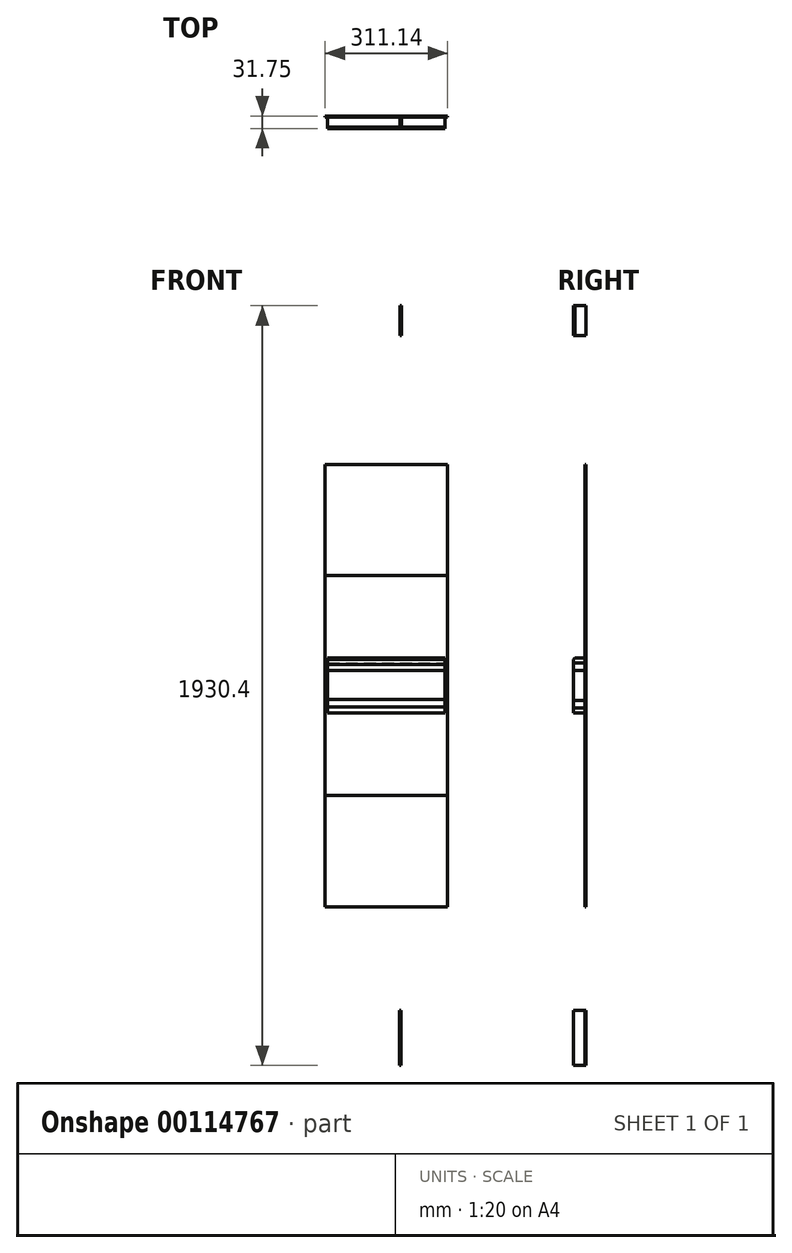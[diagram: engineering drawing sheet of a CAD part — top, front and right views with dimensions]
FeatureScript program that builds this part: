
annotation { "Feature Type Name" : "Feature", "Feature Type Description" : "" }
export const myFeature = defineFeature(function(context is Context, id is Id, definition is map)
    precondition{}
    {
        {
            var Q0;
            Q0=qCreatedBy(makeId("Front.planeOp"),FACE);
            var sketch = newSketch(context, id + "F0", { "sketchPlane" : qUnion([Q0])});
            skLineSegment(sketch, "E0.bottom", {"start": v(38.1, 965.2) * mm, "end": v(-38.1, 965.2) * mm});
            skLineSegment(sketch, "E0.top", {"start": v(38.1, -965.2) * mm, "end": v(-38.1, -965.2) * mm});
            skLineSegment(sketch, "E0.left", {"start": v(38.1, 965.2) * mm, "end": v(38.1, -965.2) * mm});
            skLineSegment(sketch, "E0.right", {"start": v(-38.1, 965.2) * mm, "end": v(-38.1, -965.2) * mm});
            skPoint(sketch, "E0.middle", {"position": v(0, 0) * mm});
            skLineSegment(sketch, "E1.bottom", {"start": v(38.1, -279.4) * mm, "end": v(38.1, -279.4) * mm});
            skLineSegment(sketch, "E2.bottom", {"start": v(38.1, -279.4) * mm, "end": v(34.93, -279.4) * mm});
            skLineSegment(sketch, "E2.top", {"start": v(38.1, -165.1) * mm, "end": v(34.93, -165.1) * mm});
            skLineSegment(sketch, "E2.left", {"start": v(38.1, -279.4) * mm, "end": v(38.1, -165.1) * mm});
            skLineSegment(sketch, "E2.right", {"start": v(34.93, -279.4) * mm, "end": v(34.93, -165.1) * mm});
            skLineSegment(sketch, "E3.bottom", {"start": v(38.1, -965.2) * mm, "end": v(34.93, -965.2) * mm});
            skLineSegment(sketch, "E3.top", {"start": v(38.1, -825.5) * mm, "end": v(34.93, -825.5) * mm});
            skLineSegment(sketch, "E3.left", {"start": v(38.1, -965.2) * mm, "end": v(38.1, -825.5) * mm});
            skLineSegment(sketch, "E3.right", {"start": v(34.93, -965.2) * mm, "end": v(34.93, -825.5) * mm});
            skLineSegment(sketch, "E4.bottom", {"start": v(38.1, 965.2) * mm, "end": v(34.92, 965.2) * mm});
            skLineSegment(sketch, "E4.top", {"start": v(38.1, 889) * mm, "end": v(34.92, 889) * mm});
            skLineSegment(sketch, "E4.left", {"start": v(38.1, 965.2) * mm, "end": v(38.1, 889) * mm});
            skLineSegment(sketch, "E4.right", {"start": v(34.92, 965.2) * mm, "end": v(34.92, 889) * mm});
            skSolve(sketch);
        }
        {
            var Q0;
            Q0=makeQuery(id+"F0.imprint","IMPRINT",FACE,{"disambiguationData":[TD([[makeQuery(id+"F0.imprint","IMPRINT",EDGE,{"derivedFrom":sQuery(id+"F0.wireOp",EDGE,"E0.bottom")}),1.0]])]});
            extrude(context, id + "F1", {"entities" : qUnion([Q0]), "depth" : 31.75 * mm});
        }
        {
            var Q0;
            Q0=qCreatedBy(makeId("Front.planeOp"),FACE);
            var sketch = newSketch(context, id + "F2", { "sketchPlane" : qUnion([Q0])});
            skLineSegment(sketch, "E5.bottom", {"start": v(149.23, -69.85) * mm, "end": v(-149.22, -69.85) * mm});
            skLineSegment(sketch, "E5.top", {"start": v(149.23, 69.85) * mm, "end": v(-149.22, 69.85) * mm});
            skLineSegment(sketch, "E5.left", {"start": v(149.23, -69.85) * mm, "end": v(149.23, 69.85) * mm});
            skLineSegment(sketch, "E5.right", {"start": v(-149.22, -69.85) * mm, "end": v(-149.22, 69.85) * mm});
            skPoint(sketch, "E5.middle", {"position": v(0, 0) * mm});
            skSolve(sketch);
        }
        {
            var Q0;
            Q0=makeQuery(id+"F2.imprint","IMPRINT",FACE,{"disambiguationData":[TD([[makeQuery(id+"F2.imprint","IMPRINT",EDGE,{"derivedFrom":sQuery(id+"F2.wireOp",EDGE,"E5.bottom")}),-1.0]])]});
            extrude(context, id + "F3", {"entities" : qUnion([Q0]), "depth" : 31.75 * mm});
        }
        {
            var Q0;
            Q0=qCreatedBy(makeId("Front.planeOp"),FACE);
            var sketch = newSketch(context, id + "F4", { "sketchPlane" : qUnion([Q0])});
            skLineSegment(sketch, "E6.bottom", {"start": v(149.23, -38.1) * mm, "end": v(-149.23, -38.1) * mm});
            skLineSegment(sketch, "E6.top", {"start": v(149.23, 38.1) * mm, "end": v(-149.23, 38.1) * mm});
            skLineSegment(sketch, "E6.left", {"start": v(149.23, -38.1) * mm, "end": v(149.23, 38.1) * mm});
            skLineSegment(sketch, "E6.right", {"start": v(-149.23, -38.1) * mm, "end": v(-149.23, 38.1) * mm});
            skPoint(sketch, "E6.middle", {"position": v(0, 0) * mm});
            skSolve(sketch);
        }
        {
            var Q0;
            Q0=makeQuery(id+"F4.imprint","IMPRINT",FACE,{"disambiguationData":[TD([[makeQuery(id+"F4.imprint","IMPRINT",EDGE,{"derivedFrom":sQuery(id+"F4.wireOp",EDGE,"E6.bottom")}),-1.0]])]});
            extrude(context, id + "F5", {"entities" : qUnion([Q0]), "depth" : 31.75 * mm});
        }
        {
            var Q0;
            Q0=qCreatedBy(makeId("Front.planeOp"),FACE);
            var sketch = newSketch(context, id + "F6", { "sketchPlane" : qUnion([Q0])});
            skLineSegment(sketch, "E7.bottom", {"start": v(149.23, -57.15) * mm, "end": v(-149.23, -57.15) * mm});
            skLineSegment(sketch, "E7.top", {"start": v(149.22, 57.15) * mm, "end": v(-149.22, 57.15) * mm});
            skLineSegment(sketch, "E7.left", {"start": v(149.23, -57.15) * mm, "end": v(149.23, 57.15) * mm});
            skLineSegment(sketch, "E7.right", {"start": v(-149.23, -57.15) * mm, "end": v(-149.23, 57.15) * mm});
            skPoint(sketch, "E7.middle", {"position": v(0, 0) * mm});
            skSolve(sketch);
        }
        {
            var Q0;
            Q0=makeQuery(id+"F6.imprint","IMPRINT",FACE,{"disambiguationData":[TD([[makeQuery(id+"F6.imprint","IMPRINT",EDGE,{"derivedFrom":sQuery(id+"F6.wireOp",EDGE,"E7.bottom")}),-1.0]])]});
            extrude(context, id + "F7", {"entities" : qUnion([Q0]), "depth" : 31.75 * mm});
        }
        {
            var Q0;
            {var subQ0=sQuery(id+"F0.wireOp",EDGE,"E0.left");Q0=makeQuery(id+"F1.opExtrude","CAP_EDGE",EDGE,{"disambiguationData":[OSD([subQ0]),TDD([makeQuery(id+"F0.imprint","IMPRINT",EDGE,{"disambiguationData":[TD([[makeQuery(id+"F0.imprint","INTERSECT",VERTEX,{"derivedFrom":[subQ0,sQuery(id+"F0.wireOp",EDGE,"E4.top"),sQuery(id+"F0.wireOp",EDGE,"E4.left")]}),-1.0]])],"derivedFrom":subQ0})])],"isStart":false});}
            var Q1;
            {var subQ0=sQuery(id+"F0.wireOp",EDGE,"E0.left");Q1=makeQuery(id+"F1.opExtrude","CAP_EDGE",EDGE,{"disambiguationData":[OSD([subQ0]),TDD([makeQuery(id+"F0.imprint","IMPRINT",EDGE,{"disambiguationData":[TD([[makeQuery(id+"F0.imprint","INTERSECT",VERTEX,{"derivedFrom":[subQ0,sQuery(id+"F0.wireOp",EDGE,"E3.top"),sQuery(id+"F0.wireOp",EDGE,"E3.left")]}),1.0]])],"derivedFrom":subQ0})])],"isStart":false});}
            chamfer(context, id + "F8", {"entities" : qUnion([Q0, Q1]), "width" : 3.17 * mm, "tangentPropagation" : true});
        }
        {
            var Q0;
            Q0=makeQuery(id+"F3.opExtrude","CAP_EDGE",EDGE,{"disambiguationData":[OSD([sQuery(id+"F2.wireOp",EDGE,"E5.top")])],"isStart":false});
            chamfer(context, id + "F9", {"entities" : qUnion([Q0]), "width" : 3.17 * mm, "tangentPropagation" : true});
        }
        {
            var Q0;
            Q0=makeQuery(id+"F5.opExtrude","CAP_EDGE",EDGE,{"disambiguationData":[OSD([sQuery(id+"F4.wireOp",EDGE,"E6.bottom")])],"isStart":false});
            chamfer(context, id + "F10", {"entities" : qUnion([Q0]), "width" : 3.17 * mm, "tangentPropagation" : true});
        }
        {
            var Q0;
            Q0=makeQuery(id+"F7.opExtrude","CAP_EDGE",EDGE,{"disambiguationData":[OSD([sQuery(id+"F6.wireOp",EDGE,"E7.bottom")])],"isStart":false});
            var Q1;
            Q1=makeQuery(id+"F7.opExtrude","CAP_EDGE",EDGE,{"disambiguationData":[OSD([sQuery(id+"F6.wireOp",EDGE,"E7.top")])],"isStart":false});
            chamfer(context, id + "F11", {"entities" : qUnion([Q0, Q1]), "width" : 3.17 * mm, "tangentPropagation" : true});
        }
        {
            var Q0;
            Q0=qCreatedBy(makeId("Front.planeOp"),FACE);
            var sketch = newSketch(context, id + "F12", { "sketchPlane" : qUnion([Q0])});
            skLineSegment(sketch, "E8.bottom", {"start": v(36.51, -965.2) * mm, "end": v(-36.51, -965.2) * mm});
            skLineSegment(sketch, "E8.top", {"start": v(36.51, 965.2) * mm, "end": v(-36.51, 965.2) * mm});
            skLineSegment(sketch, "E8.left", {"start": v(36.51, -965.2) * mm, "end": v(36.51, 965.2) * mm});
            skLineSegment(sketch, "E8.right", {"start": v(-36.51, -965.2) * mm, "end": v(-36.51, 965.2) * mm});
            skPoint(sketch, "E8.middle", {"position": v(0, 0) * mm});
            skLineSegment(sketch, "E9.bottom", {"start": v(36.51, 965.2) * mm, "end": v(33.34, 965.2) * mm});
            skLineSegment(sketch, "E9.top", {"start": v(36.51, 889) * mm, "end": v(33.34, 889) * mm});
            skLineSegment(sketch, "E9.left", {"start": v(36.51, 965.2) * mm, "end": v(36.51, 889) * mm});
            skLineSegment(sketch, "E9.right", {"start": v(33.34, 965.2) * mm, "end": v(33.34, 889) * mm});
            skLineSegment(sketch, "E10.bottom", {"start": v(36.51, -965.2) * mm, "end": v(33.34, -965.2) * mm});
            skLineSegment(sketch, "E10.top", {"start": v(36.51, -825.5) * mm, "end": v(33.34, -825.5) * mm});
            skLineSegment(sketch, "E10.left", {"start": v(36.51, -965.2) * mm, "end": v(36.51, -825.5) * mm});
            skLineSegment(sketch, "E10.right", {"start": v(33.34, -965.2) * mm, "end": v(33.34, -825.5) * mm});
            skLineSegment(sketch, "E11.bottom", {"start": v(36.51, -165.1) * mm, "end": v(33.34, -165.1) * mm});
            skLineSegment(sketch, "E11.top", {"start": v(36.51, -279.4) * mm, "end": v(33.34, -279.4) * mm});
            skLineSegment(sketch, "E11.left", {"start": v(36.51, -165.1) * mm, "end": v(36.51, -279.4) * mm});
            skLineSegment(sketch, "E11.right", {"start": v(33.34, -165.1) * mm, "end": v(33.34, -279.4) * mm});
            skSolve(sketch);
        }
        {
            var Q0;
            Q0=makeQuery(id+"F12.imprint","IMPRINT",FACE,{"disambiguationData":[TD([[makeQuery(id+"F12.imprint","IMPRINT",EDGE,{"derivedFrom":sQuery(id+"F12.wireOp",EDGE,"E8.bottom")}),-1.0]])]});
            extrude(context, id + "F13", {"entities" : qUnion([Q0]), "depth" : 31.75 * mm});
        }
        {
            var Q0;
            {var subQ0=sQuery(id+"F12.wireOp",EDGE,"E8.left");Q0=makeQuery(id+"F13.opExtrude","CAP_EDGE",EDGE,{"disambiguationData":[OSD([subQ0]),TDD([makeQuery(id+"F12.imprint","IMPRINT",EDGE,{"disambiguationData":[TD([[makeQuery(id+"F12.imprint","INTERSECT",VERTEX,{"derivedFrom":[subQ0,sQuery(id+"F12.wireOp",EDGE,"E9.top"),sQuery(id+"F12.wireOp",EDGE,"E9.left")]}),1.0]])],"derivedFrom":subQ0})])],"isStart":true});}
            var Q1;
            {var subQ0=sQuery(id+"F12.wireOp",EDGE,"E8.left");Q1=makeQuery(id+"F13.opExtrude","CAP_EDGE",EDGE,{"disambiguationData":[OSD([subQ0]),TDD([makeQuery(id+"F12.imprint","IMPRINT",EDGE,{"disambiguationData":[TD([[makeQuery(id+"F12.imprint","INTERSECT",VERTEX,{"derivedFrom":[subQ0,sQuery(id+"F12.wireOp",EDGE,"E10.top"),sQuery(id+"F12.wireOp",EDGE,"E10.left")]}),-1.0]])],"derivedFrom":subQ0})])],"isStart":true});}
            chamfer(context, id + "F14", {"entities" : qUnion([Q0, Q1]), "width" : 3.17 * mm, "tangentPropagation" : true});
        }
        {
            var Q0;
            Q0=qCreatedBy(makeId("Front.planeOp"),FACE);
            var sketch = newSketch(context, id + "F15", { "sketchPlane" : qUnion([Q0])});
            skLineSegment(sketch, "E12.bottom", {"start": v(155.57, -561.98) * mm, "end": v(-155.58, -561.98) * mm});
            skLineSegment(sketch, "E12.top", {"start": v(155.58, 561.98) * mm, "end": v(-155.57, 561.98) * mm});
            skLineSegment(sketch, "E12.left", {"start": v(155.57, -561.98) * mm, "end": v(155.58, 561.98) * mm});
            skLineSegment(sketch, "E12.right", {"start": v(-155.58, -561.98) * mm, "end": v(-155.57, 561.98) * mm});
            skPoint(sketch, "E12.middle", {"position": v(0, 0) * mm});
            skSolve(sketch);
        }
        {
            var Q0;
            Q0=makeQuery(id+"F15.imprint","IMPRINT",FACE,{"disambiguationData":[TD([[makeQuery(id+"F15.imprint","IMPRINT",EDGE,{"derivedFrom":sQuery(id+"F15.wireOp",EDGE,"E12.bottom")}),-1.0]])]});
            extrude(context, id + "F16", {"entities" : qUnion([Q0]), "depth" : 3.17 * mm});
        }
        {
            var Q0;
            Q0=qCreatedBy(makeId("Front.planeOp"),FACE);
            var sketch = newSketch(context, id + "F17", { "sketchPlane" : qUnion([Q0])});
            skLineSegment(sketch, "E13.bottom", {"start": v(155.57, -279.4) * mm, "end": v(-155.58, -279.4) * mm});
            skLineSegment(sketch, "E13.top", {"start": v(155.57, 279.4) * mm, "end": v(-155.58, 279.4) * mm});
            skLineSegment(sketch, "E13.left", {"start": v(155.57, -279.4) * mm, "end": v(155.58, 279.4) * mm});
            skLineSegment(sketch, "E13.right", {"start": v(-155.58, -279.4) * mm, "end": v(-155.58, 279.4) * mm});
            skPoint(sketch, "E13.middle", {"position": v(0, 0) * mm});
            skSolve(sketch);
        }
        {
            var Q0;
            Q0=makeQuery(id+"F17.imprint","IMPRINT",FACE,{"disambiguationData":[TD([[makeQuery(id+"F17.imprint","IMPRINT",EDGE,{"derivedFrom":sQuery(id+"F17.wireOp",EDGE,"E13.bottom")}),-1.0]])]});
            extrude(context, id + "F18", {"entities" : qUnion([Q0]), "depth" : 3.17 * mm});
        }
    });
